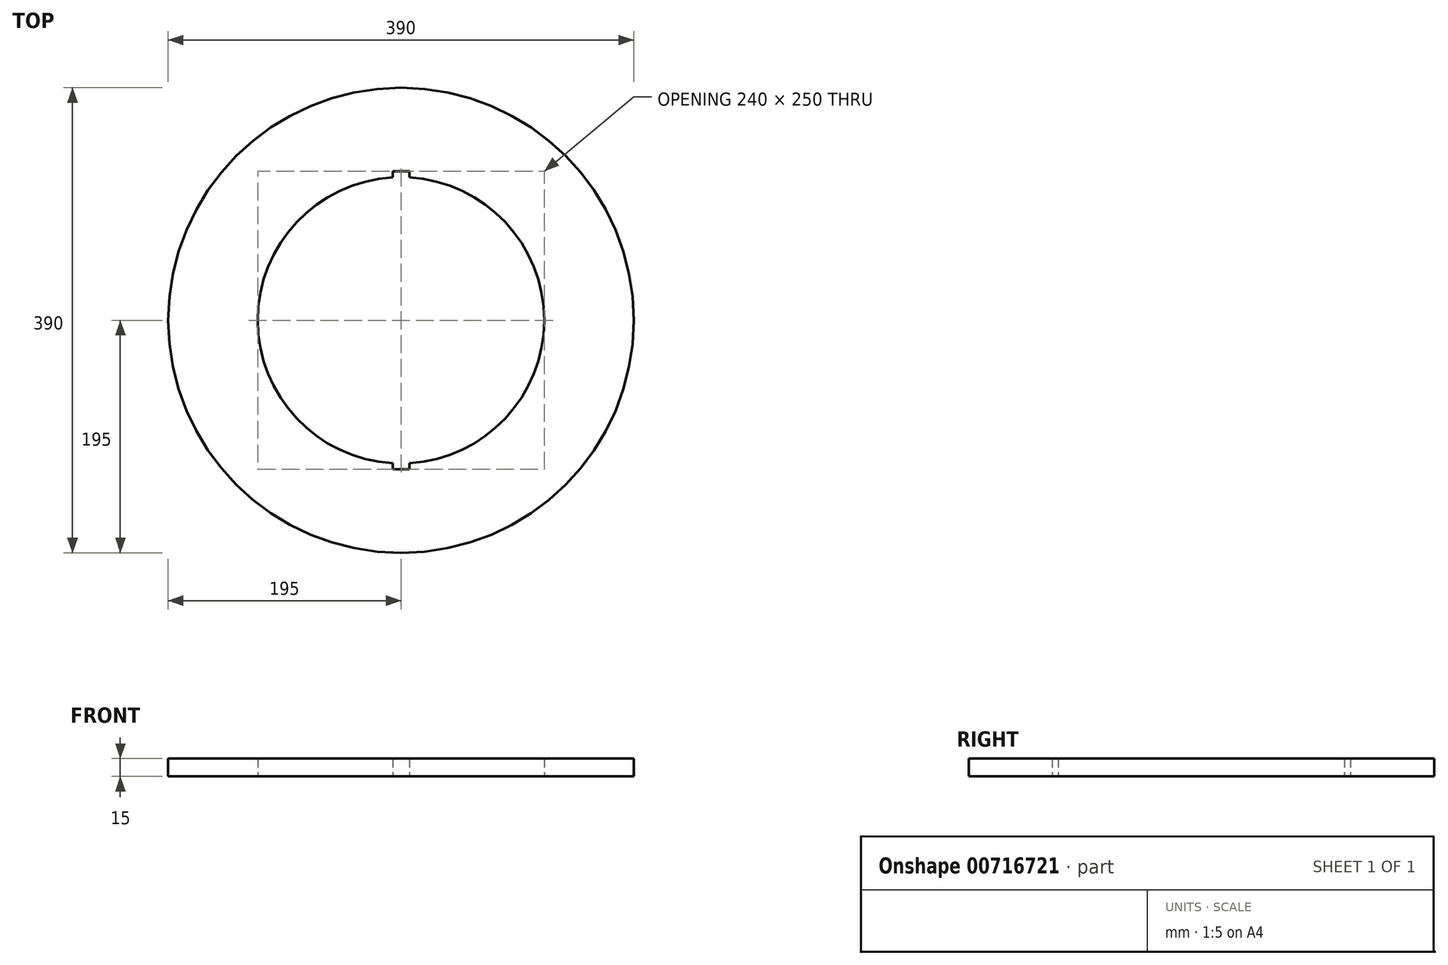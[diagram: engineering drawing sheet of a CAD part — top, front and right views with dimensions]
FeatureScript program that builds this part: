
annotation { "Feature Type Name" : "Feature", "Feature Type Description" : "" }
export const myFeature = defineFeature(function(context is Context, id is Id, definition is map)
    precondition{}
    {
        {
            var Q0;
            Q0=qCreatedBy(makeId("Top.planeOp"),FACE);
            var sketch = newSketch(context, id + "F0", { "sketchPlane" : qUnion([Q0])});
            skCircle(sketch, "E0", {"center": v(0, 0) * mm, "radius": 120 * mm});
            skCircle(sketch, "E1", {"center": v(0, 0) * mm, "radius": 195 * mm});
            skLineSegment(sketch, "E2.bottom", {"start": v(7, 125) * mm, "end": v(-7, 125) * mm});
            skLineSegment(sketch, "E2.top", {"start": v(7, 115) * mm, "end": v(-7, 115) * mm});
            skLineSegment(sketch, "E2.left", {"start": v(7, 125) * mm, "end": v(7, 115) * mm});
            skLineSegment(sketch, "E2.right", {"start": v(-7, 125) * mm, "end": v(-7, 115) * mm});
            skPoint(sketch, "E2.middle", {"position": v(0, 120) * mm});
            skLineSegment(sketch, "E3.1.0", {"start": v(-7, -125) * mm, "end": v(7, -125) * mm});
            skLineSegment(sketch, "E3.1.1", {"start": v(-7, -115) * mm, "end": v(7, -115) * mm});
            skLineSegment(sketch, "E3.1.2", {"start": v(-7, -125) * mm, "end": v(-7, -115) * mm});
            skLineSegment(sketch, "E3.1.3", {"start": v(7, -125) * mm, "end": v(7, -115) * mm});
            skPoint(sketch, "E3.1.4", {"position": v(0, -120) * mm});
            skSolve(sketch);
        }
        {
            var Q0;
            Q0=makeQuery(id+"F0.imprint","IMPRINT",FACE,{"disambiguationData":[TD([[makeQuery(id+"F0.imprint","IMPRINT",EDGE,{"derivedFrom":sQuery(id+"F0.wireOp",EDGE,"E0")}),-1.0]])]});
            extrude(context, id + "F1", {"entities" : qUnion([Q0]), "depth" : 15 * mm, "offsetDistance" : 25 * mm});
        }
    });
